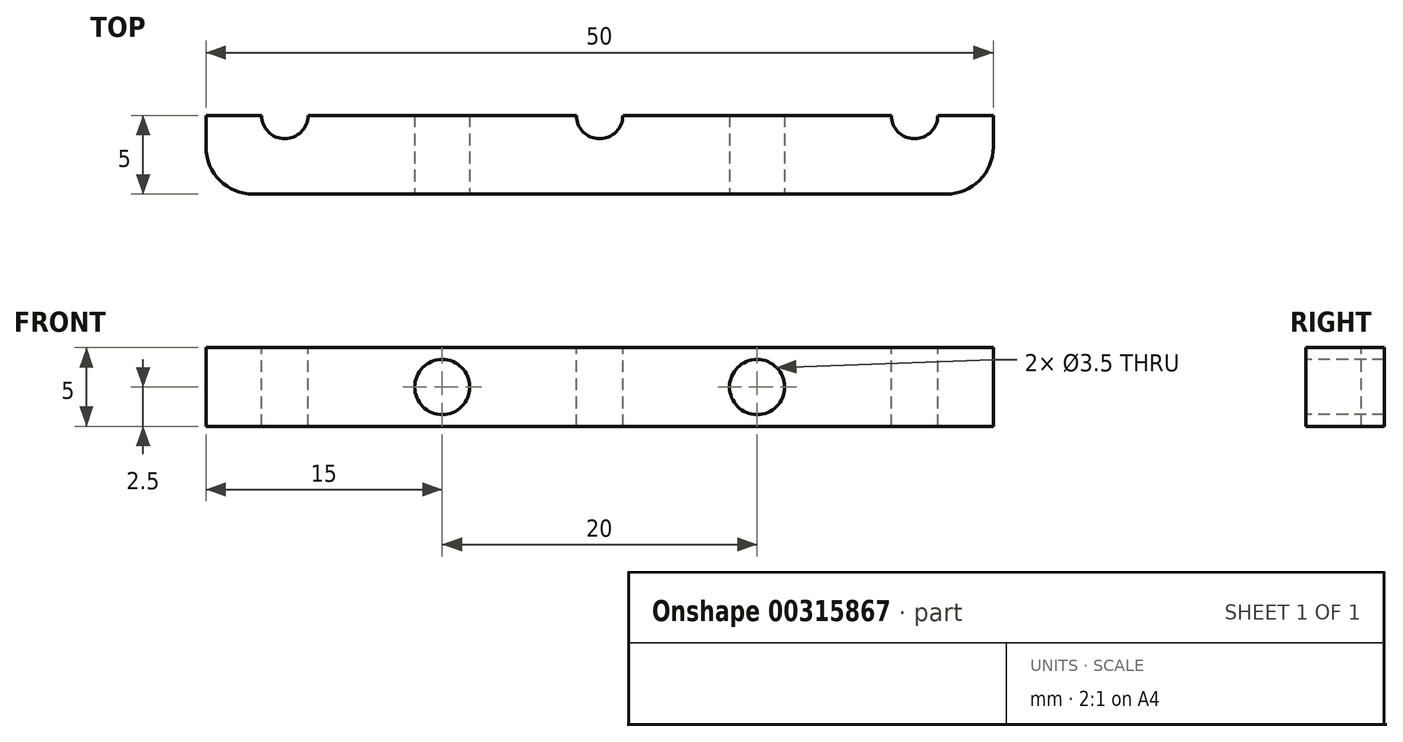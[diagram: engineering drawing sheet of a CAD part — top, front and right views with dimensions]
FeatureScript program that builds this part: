
annotation { "Feature Type Name" : "Feature", "Feature Type Description" : "" }
export const myFeature = defineFeature(function(context is Context, id is Id, definition is map)
    precondition{}
    {
        {
            var Q0;
            Q0=qCreatedBy(makeId("Front.planeOp"),FACE);
            var sketch = newSketch(context, id + "F0", { "sketchPlane" : qUnion([Q0])});
            skLineSegment(sketch, "E0.bottom", {"start": v(25, 2.5) * mm, "end": v(-25, 2.5) * mm});
            skLineSegment(sketch, "E0.top", {"start": v(25, -2.5) * mm, "end": v(-25, -2.5) * mm});
            skLineSegment(sketch, "E0.left", {"start": v(25, 2.5) * mm, "end": v(25, -2.5) * mm});
            skLineSegment(sketch, "E0.right", {"start": v(-25, 2.5) * mm, "end": v(-25, -2.5) * mm});
            skPoint(sketch, "E0.middle", {"position": v(0, 0) * mm});
            skPoint(sketch, "E1", {"position": v(-10, 0) * mm});
            skPoint(sketch, "E2", {"position": v(10, 0) * mm});
            skSolve(sketch);
        }
        {
            var Q0;
            Q0=makeQuery(id+"F0.imprint","IMPRINT",FACE,{"disambiguationData":[TD([[makeQuery(id+"F0.imprint","IMPRINT",EDGE,{"derivedFrom":sQuery(id+"F0.wireOp",EDGE,"E0.bottom")}),1.0]])]});
            extrude(context, id + "F1", {"entities" : qUnion([Q0]), "oppositeDirection" : true, "depth" : 5 * mm});
        }
        {
            var Q0;
            Q0=sQuery(id+"F0.wireOp",VERTEX,"E1");
            var Q1;
            Q1=sQuery(id+"F0.wireOp",VERTEX,"E2");
            var Q2;
            Q2=makeQuery(id+"F1.opExtrude","SWEPT_BODY",BODY,{"disambiguationData":[OSD([sQuery(id+"F0.wireOp",EDGE,"E0.bottom"),sQuery(id+"F0.wireOp",EDGE,"E0.top"),sQuery(id+"F0.wireOp",EDGE,"E0.left"),sQuery(id+"F0.wireOp",EDGE,"E0.right")])]});
            hole(context, id + "F2", {"style" : HoleStyle.SIMPLE, "endStyle" : HoleEndStyle.THROUGH, "holeDiameter" : 3.5 * mm, "isTappedThrough" : true, "tappedDepth" : 12 * mm, "tapClearance" : 3, "locations" : qUnion([Q0, Q1]), "scope" : qUnion([Q2])});
        }
        {
            var Q0;
            Q0=makeQuery(id+"F1.opExtrude","CAP_EDGE",EDGE,{"disambiguationData":[OSD([sQuery(id+"F0.wireOp",EDGE,"E0.right")])],"isStart":true});
            var Q1;
            Q1=makeQuery(id+"F1.opExtrude","CAP_EDGE",EDGE,{"disambiguationData":[OSD([sQuery(id+"F0.wireOp",EDGE,"E0.left")])],"isStart":true});
            fillet(context, id + "F3", {"entities" : qUnion([Q0, Q1]), "radius" : 3 * mm, "tangentPropagation" : true, "allowEdgeOverflow" : false});
        }
        {
            var Q0;
            Q0=makeQuery(id+"F1.opExtrude","SWEPT_FACE",FACE,{"disambiguationData":[OSD([sQuery(id+"F0.wireOp",EDGE,"E0.bottom")])]});
            var sketch = newSketch(context, id + "F4", { "sketchPlane" : qUnion([Q0])});
            skPoint(sketch, "E3", {"position": v(0, 5) * mm});
            skPoint(sketch, "E4", {"position": v(20, 5) * mm});
            skPoint(sketch, "E5", {"position": v(-20, 5) * mm});
            skSolve(sketch);
        }
        {
            var Q0;
            Q0=sQuery(id+"F4.wireOp",VERTEX,"E5");
            var Q1;
            Q1=sQuery(id+"F4.wireOp",VERTEX,"E3");
            var Q2;
            Q2=sQuery(id+"F4.wireOp",VERTEX,"E4");
            var Q3;
            Q3=makeQuery(id+"F1.opExtrude","SWEPT_BODY",BODY,{"disambiguationData":[OSD([sQuery(id+"F0.wireOp",EDGE,"E0.bottom"),sQuery(id+"F0.wireOp",EDGE,"E0.top"),sQuery(id+"F0.wireOp",EDGE,"E0.left"),sQuery(id+"F0.wireOp",EDGE,"E0.right")])]});
            hole(context, id + "F5", {"style" : HoleStyle.SIMPLE, "endStyle" : HoleEndStyle.THROUGH, "holeDiameter" : 2.95 * mm, "isTappedThrough" : true, "tappedDepth" : 12 * mm, "tapClearance" : 3, "locations" : qUnion([Q0, Q1, Q2]), "scope" : qUnion([Q3])});
        }
    });
